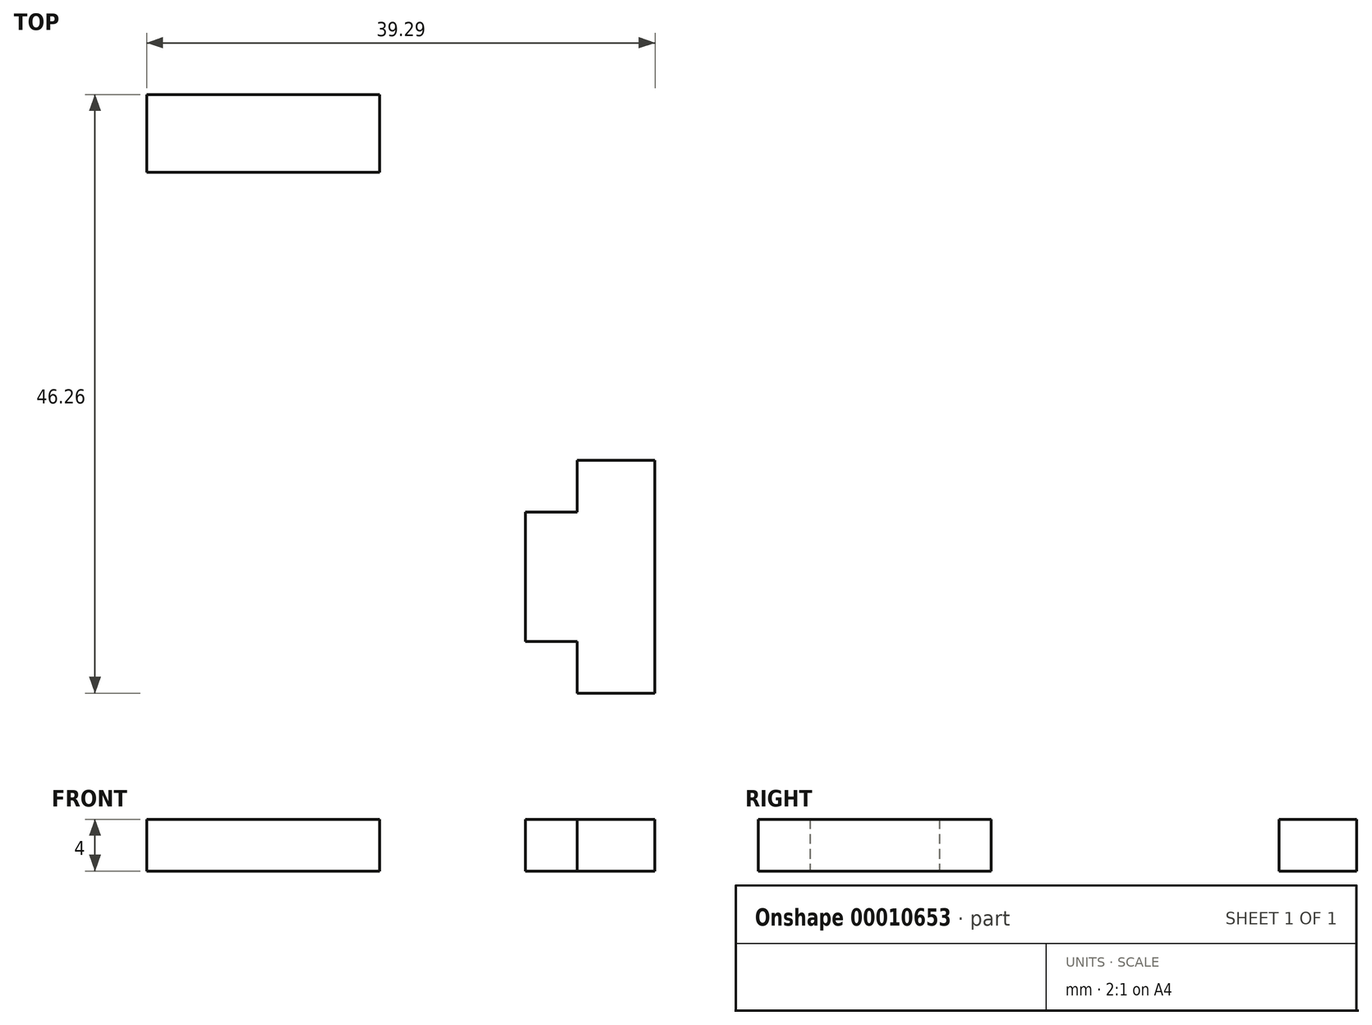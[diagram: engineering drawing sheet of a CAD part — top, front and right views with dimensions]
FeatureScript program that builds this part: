
annotation { "Feature Type Name" : "Feature", "Feature Type Description" : "" }
export const myFeature = defineFeature(function(context is Context, id is Id, definition is map)
    precondition{}
    {
        {
            var Q0;
            Q0=qCreatedBy(makeId("Top.planeOp"),FACE);
            var sketch = newSketch(context, id + "F0", { "sketchPlane" : qUnion([Q0])});
            skLineSegment(sketch, "E0.bottom", {"start": v(0, 0) * mm, "end": v(-18, 0) * mm});
            skLineSegment(sketch, "E0.top", {"start": v(0, -6) * mm, "end": v(-18, -6) * mm});
            skLineSegment(sketch, "E0.left", {"start": v(0, 0) * mm, "end": v(0, -6) * mm});
            skLineSegment(sketch, "E0.right", {"start": v(-18, 0) * mm, "end": v(-18, -6) * mm});
            skSolve(sketch);
        }
        {
            var Q0;
            Q0=makeQuery(id+"F0.imprint","IMPRINT",FACE,{"disambiguationData":[TD([[makeQuery(id+"F0.imprint","IMPRINT",EDGE,{"derivedFrom":sQuery(id+"F0.wireOp",EDGE,"E0.bottom")}),1.0]])]});
            extrude(context, id + "F1", {"entities" : qUnion([Q0]), "depth" : 4 * mm});
        }
        {
            var Q0;
            Q0=qCreatedBy(makeId("Top.planeOp"),FACE);
            var sketch = newSketch(context, id + "F2", { "sketchPlane" : qUnion([Q0])});
            skLineSegment(sketch, "E1", {"start": v(21.29, -28.26) * mm, "end": v(21.29, -46.26) * mm});
            skLineSegment(sketch, "E2", {"start": v(21.29, -46.26) * mm, "end": v(15.29, -46.26) * mm});
            skLineSegment(sketch, "E3", {"start": v(15.29, -46.26) * mm, "end": v(15.29, -42.26) * mm});
            skLineSegment(sketch, "E4", {"start": v(15.29, -42.26) * mm, "end": v(11.29, -42.26) * mm});
            skLineSegment(sketch, "E5", {"start": v(11.29, -42.26) * mm, "end": v(11.29, -32.26) * mm});
            skLineSegment(sketch, "E6", {"start": v(11.29, -32.26) * mm, "end": v(15.29, -32.26) * mm});
            skLineSegment(sketch, "E7", {"start": v(15.29, -32.26) * mm, "end": v(15.29, -28.26) * mm});
            skLineSegment(sketch, "E8", {"start": v(15.29, -28.26) * mm, "end": v(21.29, -28.26) * mm});
            skSolve(sketch);
        }
        {
            var Q0;
            Q0=makeQuery(id+"F2.imprint","IMPRINT",FACE,{"disambiguationData":[TD([[makeQuery(id+"F2.imprint","IMPRINT",EDGE,{"derivedFrom":sQuery(id+"F2.wireOp",EDGE,"E1")}),-1.0]])]});
            extrude(context, id + "F3", {"entities" : qUnion([Q0]), "depth" : 4 * mm});
        }
    });
